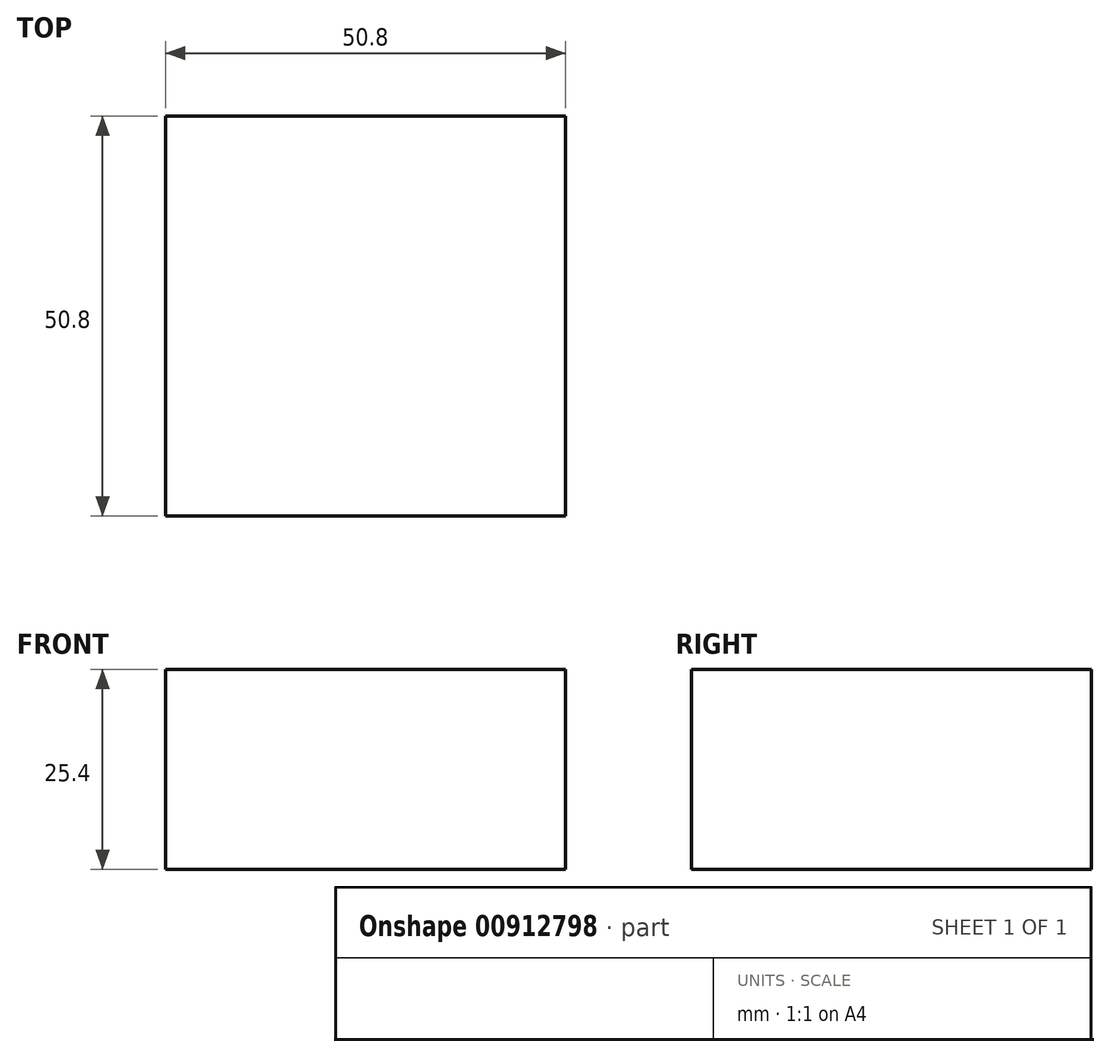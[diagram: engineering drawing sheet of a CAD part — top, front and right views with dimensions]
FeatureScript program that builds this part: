
annotation { "Feature Type Name" : "Feature", "Feature Type Description" : "" }
export const myFeature = defineFeature(function(context is Context, id is Id, definition is map)
    precondition{}
    {
        {
            var Q0;
            Q0=qCreatedBy(makeId("Top.planeOp"),FACE);
            var sketch = newSketch(context, id + "F0", { "sketchPlane" : qUnion([Q0])});
            skLineSegment(sketch, "E0", {"start": v(0, 0) * mm, "end": v(0, 50.8) * mm});
            skLineSegment(sketch, "E1", {"start": v(0, 50.8) * mm, "end": v(50.8, 50.8) * mm});
            skLineSegment(sketch, "E2", {"start": v(50.8, 50.8) * mm, "end": v(50.8, 0) * mm});
            skLineSegment(sketch, "E3", {"start": v(50.8, 0) * mm, "end": v(0, 0) * mm});
            skSolve(sketch);
        }
        {
            var Q0;
            Q0 = qSketchRegion(id + "F0", true);
            extrude(context, id + "F1", {"entities" : qUnion([Q0]), "depth" : 25.4 * mm, "offsetDistance" : 25.4 * mm});
        }
    });
